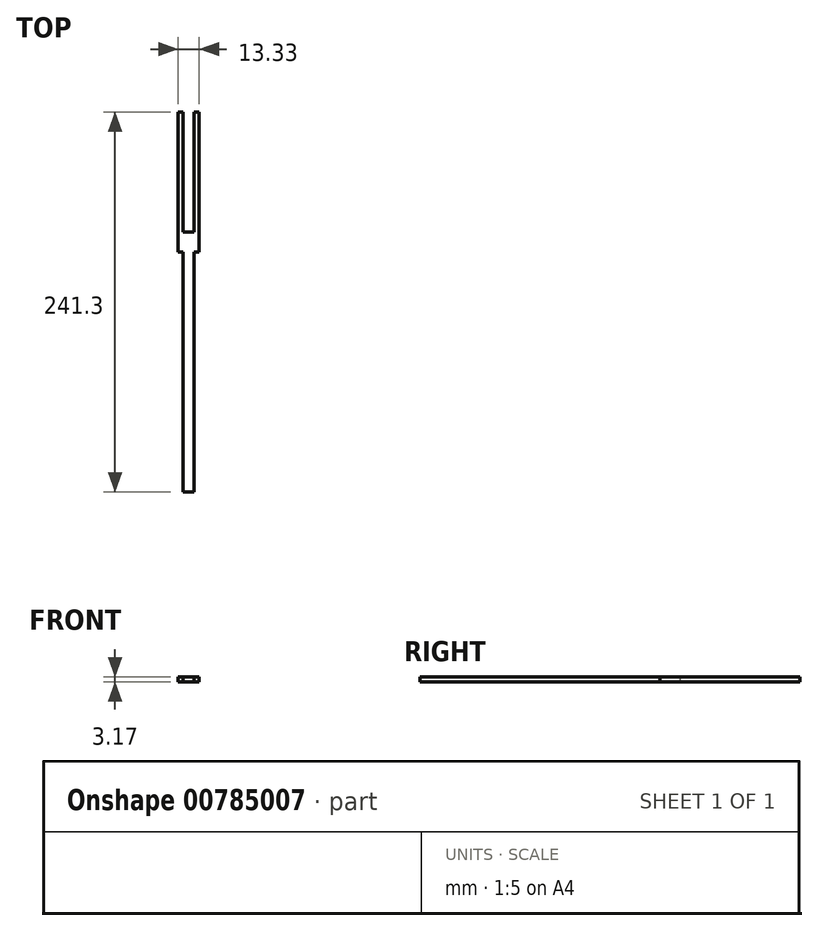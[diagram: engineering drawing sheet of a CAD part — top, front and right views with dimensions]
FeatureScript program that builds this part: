
annotation { "Feature Type Name" : "Feature", "Feature Type Description" : "" }
export const myFeature = defineFeature(function(context is Context, id is Id, definition is map)
    precondition{}
    {
        {
            var Q0;
            Q0=qCreatedBy(makeId("Top.planeOp"),FACE);
            var sketch = newSketch(context, id + "F0", { "sketchPlane" : qUnion([Q0])});
            skLineSegment(sketch, "E0.bottom", {"start": v(-63.15, 127.98) * mm, "end": v(-56.16, 127.98) * mm});
            skLineSegment(sketch, "E0.top", {"start": v(-63.15, -37.12) * mm, "end": v(-56.16, -37.12) * mm});
            skLineSegment(sketch, "E0.left", {"start": v(-63.15, 127.98) * mm, "end": v(-63.15, -37.12) * mm});
            skLineSegment(sketch, "E0.right", {"start": v(-56.16, 127.98) * mm, "end": v(-56.16, -37.12) * mm});
            skLineSegment(sketch, "E1.bottom", {"start": v(-56.16, 115.28) * mm, "end": v(-52.99, 115.28) * mm});
            skLineSegment(sketch, "E1.top", {"start": v(-56.16, 204.18) * mm, "end": v(-52.99, 204.18) * mm});
            skLineSegment(sketch, "E1.left", {"start": v(-56.16, 115.28) * mm, "end": v(-56.16, 204.18) * mm});
            skLineSegment(sketch, "E1.right", {"start": v(-52.99, 115.28) * mm, "end": v(-52.99, 204.18) * mm});
            skLineSegment(sketch, "E2.bottom", {"start": v(-63.15, 115.28) * mm, "end": v(-66.32, 115.28) * mm});
            skLineSegment(sketch, "E2.top", {"start": v(-63.15, 204.18) * mm, "end": v(-66.32, 204.18) * mm});
            skLineSegment(sketch, "E2.left", {"start": v(-63.15, 115.28) * mm, "end": v(-63.15, 204.18) * mm});
            skLineSegment(sketch, "E2.right", {"start": v(-66.32, 115.28) * mm, "end": v(-66.32, 204.18) * mm});
            skSolve(sketch);
        }
        {
            var Q0;
            {var subQ3=sQuery(id+"F0.wireOp",EDGE,"E2.bottom");Q0=makeQuery(id+"F0.imprint","IMPRINT",FACE,{"disambiguationData":[TD([[makeQuery(id+"F0.imprint","IMPRINT",EDGE,{"derivedFrom":subQ3}),-1.0]])]});}
            var Q1;
            {var subQ3=sQuery(id+"F0.wireOp",EDGE,"E1.bottom");Q1=makeQuery(id+"F0.imprint","IMPRINT",FACE,{"disambiguationData":[TD([[makeQuery(id+"F0.imprint","IMPRINT",EDGE,{"derivedFrom":subQ3}),1.0]])]});}
            var Q2;
            {var subQ2=sQuery(id+"F0.wireOp",EDGE,"E0.bottom");Q2=makeQuery(id+"F0.imprint","IMPRINT",FACE,{"disambiguationData":[TD([[makeQuery(id+"F0.imprint","IMPRINT",EDGE,{"derivedFrom":subQ2}),-1.0]])]});}
            extrude(context, id + "F1", {"entities" : qUnion([Q0, Q1, Q2]), "depth" : 3.17 * mm, "offsetDistance" : 25.4 * mm});
        }
    });
